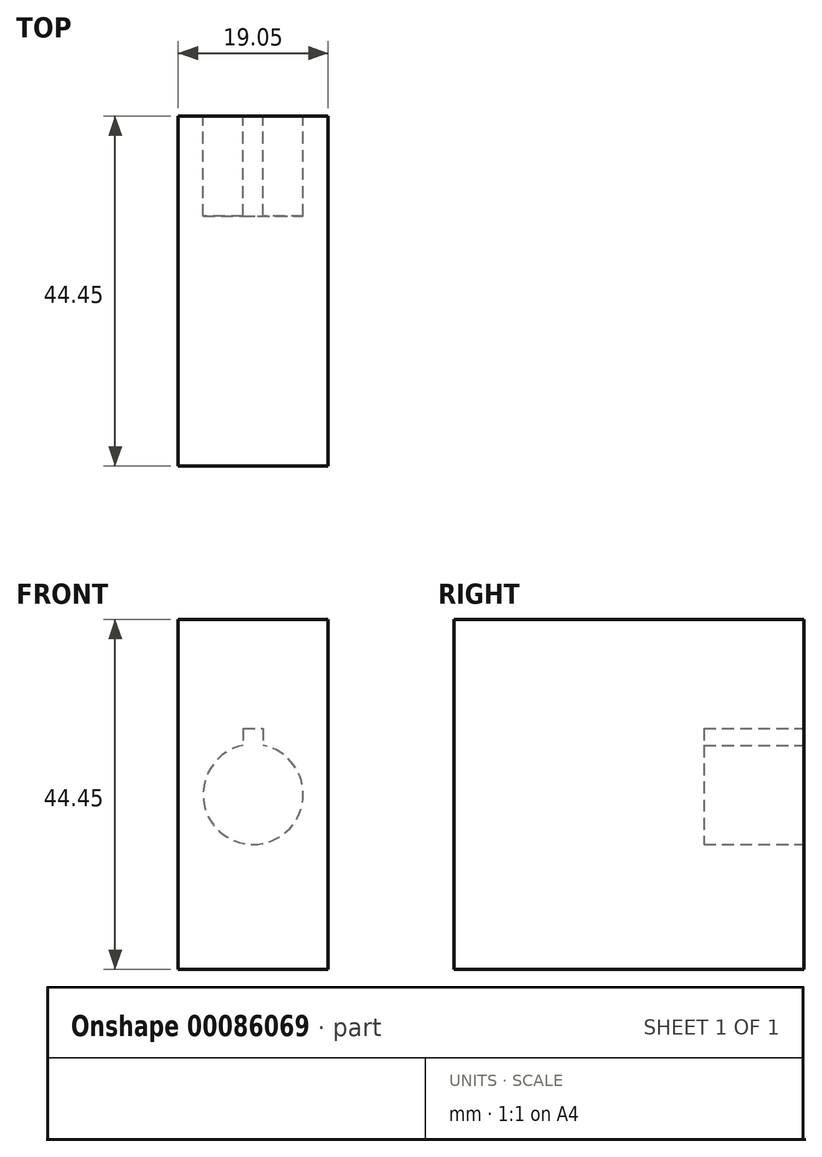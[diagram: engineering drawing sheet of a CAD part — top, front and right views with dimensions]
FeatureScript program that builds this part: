
annotation { "Feature Type Name" : "Feature", "Feature Type Description" : "" }
export const myFeature = defineFeature(function(context is Context, id is Id, definition is map)
    precondition{}
    {
        {
            var Q0;
            Q0=qCreatedBy(makeId("Front.planeOp"),FACE);
            var sketch = newSketch(context, id + "F0", { "sketchPlane" : qUnion([Q0])});
            skArc(sketch, "E0", {"start": v(-114.82, 0.1) * mm, "mid": v(-113.55, -12.47) * mm, "end": v(-112.28, 0.1) * mm});
            skLineSegment(sketch, "E1.bottom", {"start": v(-114.82, 2.23) * mm, "end": v(-112.28, 2.23) * mm});
            skLineSegment(sketch, "E1.left", {"start": v(-114.82, 2.23) * mm, "end": v(-114.82, 0.1) * mm});
            skLineSegment(sketch, "E1.right", {"start": v(-112.28, 2.23) * mm, "end": v(-112.28, 0.1) * mm});
            skPoint(sketch, "E1.top.end.orphan", {"position": v(-112.28, -14.47) * mm});
            skPoint(sketch, "E2.trimOffspring.end.orphan", {"position": v(-114.82, -14.47) * mm});
            skLineSegment(sketch, "E3", {"start": v(-113.55, -6.12) * mm, "end": v(-113.55, 16.1) * mm});
            skLineSegment(sketch, "E4", {"start": v(-113.55, -6.12) * mm, "end": v(-113.55, -28.35) * mm});
            skPoint(sketch, "E4.endSnap0", {"position": v(-113.55, -12.47) * mm});
            skLineSegment(sketch, "E5.bottom", {"start": v(-104.02, 16.1) * mm, "end": v(-123.07, 16.1) * mm});
            skLineSegment(sketch, "E5.top", {"start": v(-104.02, -28.35) * mm, "end": v(-123.07, -28.35) * mm});
            skLineSegment(sketch, "E5.left", {"start": v(-104.02, 16.1) * mm, "end": v(-104.02, -28.35) * mm});
            skLineSegment(sketch, "E5.right", {"start": v(-123.07, 16.1) * mm, "end": v(-123.07, -28.35) * mm});
            skSolve(sketch);
        }
        {
            var Q0;
            {var subQ5=sQuery(id+"F0.wireOp",EDGE,"E1.left");Q0=makeQuery(id+"F0.imprint","IMPRINT",FACE,{"disambiguationData":[TD([[makeQuery(id+"F0.imprint","IMPRINT",EDGE,{"derivedFrom":subQ5}),-1.0]])]});}
            var Q1;
            {var subQ6=sQuery(id+"F0.wireOp",EDGE,"E1.right");Q1=makeQuery(id+"F0.imprint","IMPRINT",FACE,{"disambiguationData":[TD([[makeQuery(id+"F0.imprint","IMPRINT",EDGE,{"derivedFrom":subQ6}),1.0]])]});}
            var Q2;
            {var subQ5=sQuery(id+"F0.wireOp",EDGE,"E1.right");Q2=makeQuery(id+"F0.imprint","IMPRINT",FACE,{"disambiguationData":[TD([[makeQuery(id+"F0.imprint","IMPRINT",EDGE,{"derivedFrom":subQ5}),-1.0]])]});}
            var Q3;
            {var subQ5=sQuery(id+"F0.wireOp",EDGE,"E1.left");Q3=makeQuery(id+"F0.imprint","IMPRINT",FACE,{"disambiguationData":[TD([[makeQuery(id+"F0.imprint","IMPRINT",EDGE,{"derivedFrom":subQ5}),1.0]])]});}
            extrude(context, id + "F1", {"entities" : qUnion([Q0, Q1, Q2, Q3]), "depth" : 44.45 * mm});
        }
        {
            var Q0;
            {var subQ5=sQuery(id+"F0.wireOp",EDGE,"E1.right");Q0=makeQuery(id+"F0.imprint","IMPRINT",FACE,{"disambiguationData":[TD([[makeQuery(id+"F0.imprint","IMPRINT",EDGE,{"derivedFrom":subQ5}),-1.0]])]});}
            var Q1;
            {var subQ5=sQuery(id+"F0.wireOp",EDGE,"E1.left");Q1=makeQuery(id+"F0.imprint","IMPRINT",FACE,{"disambiguationData":[TD([[makeQuery(id+"F0.imprint","IMPRINT",EDGE,{"derivedFrom":subQ5}),1.0]])]});}
            extrude(context, id + "F2", {"entities" : qUnion([Q0, Q1]), "operationType" : NewBodyOperationType.REMOVE, "depth" : 12.7 * mm});
        }
    });
